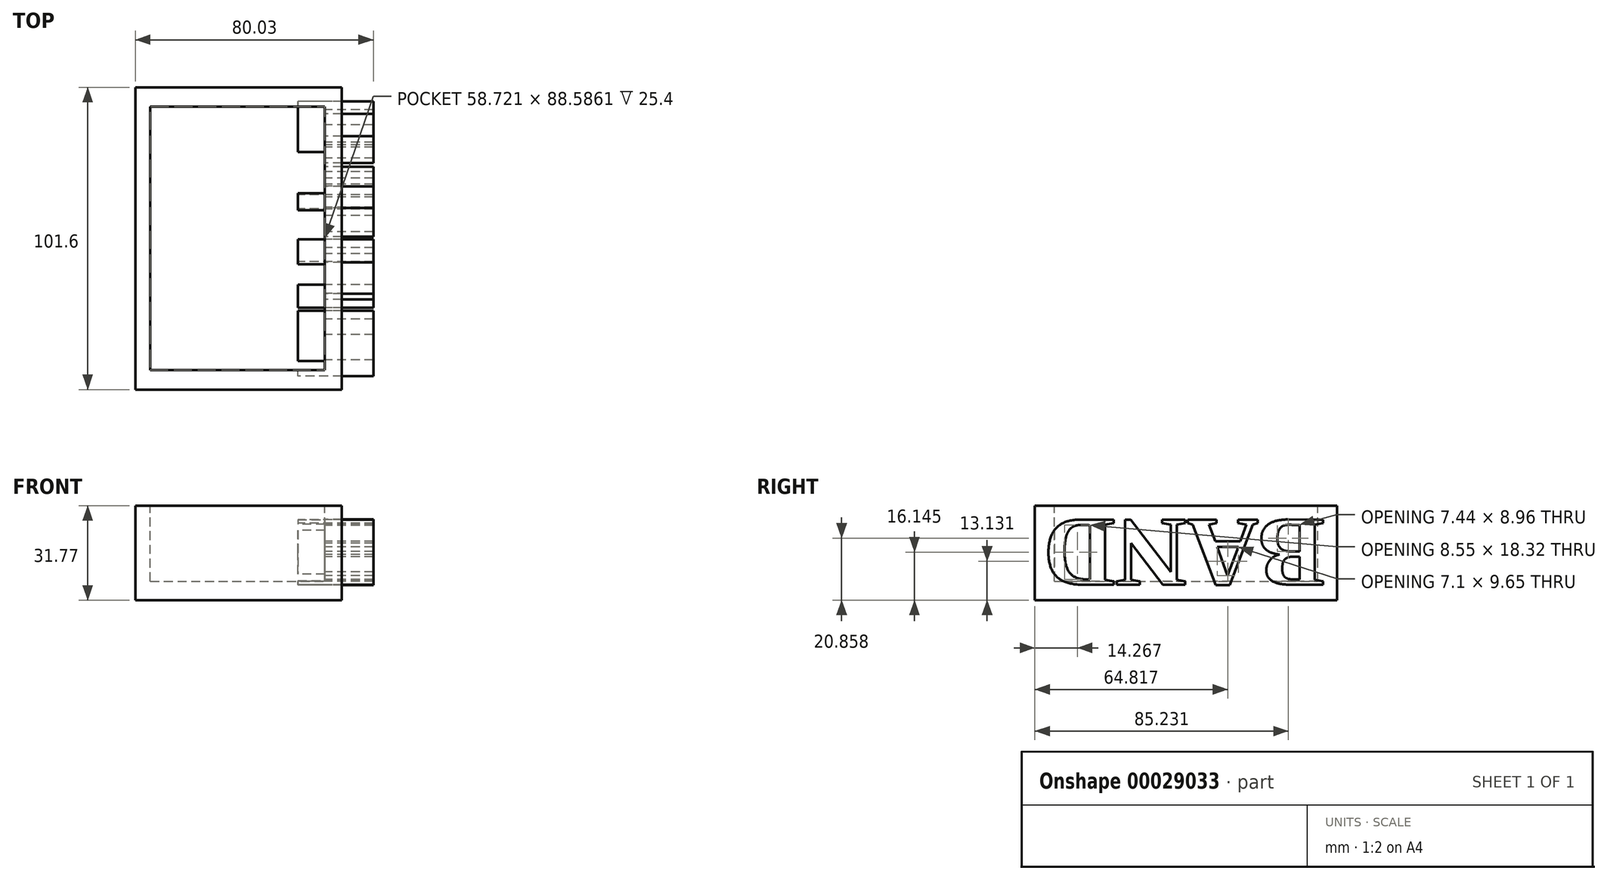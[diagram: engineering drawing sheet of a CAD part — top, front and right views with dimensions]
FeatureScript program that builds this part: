
annotation { "Feature Type Name" : "Feature", "Feature Type Description" : "" }
export const myFeature = defineFeature(function(context is Context, id is Id, definition is map)
    precondition{}
    {
        {
            var Q0;
            Q0=qCreatedBy(makeId("Front.planeOp"),FACE);
            var sketch = newSketch(context, id + "F0", { "sketchPlane" : qUnion([Q0])});
            skLineSegment(sketch, "E0.bottom", {"start": v(0, 0) * mm, "end": v(69.42, 0) * mm});
            skLineSegment(sketch, "E0.top", {"start": v(0, -19.07) * mm, "end": v(69.42, -19.07) * mm});
            skLineSegment(sketch, "E0.left", {"start": v(0, 0) * mm, "end": v(0, -19.07) * mm});
            skLineSegment(sketch, "E0.right", {"start": v(69.42, 0) * mm, "end": v(69.42, -19.07) * mm});
            skSolve(sketch);
        }
        {
            var Q0;
            Q0=makeQuery(id+"F0.imprint","IMPRINT",FACE,{"disambiguationData":[TD([[makeQuery(id+"F0.imprint","IMPRINT",EDGE,{"derivedFrom":sQuery(id+"F0.wireOp",EDGE,"E0.bottom")}),-1.0]])]});
            extrude(context, id + "F1", {"entities" : qUnion([Q0]), "depth" : 101.6 * mm});
        }
        {
            var Q0;
            Q0=makeQuery(id+"F1.opExtrude","SWEPT_BODY",BODY,{"disambiguationData":[OSD([sQuery(id+"F0.wireOp",EDGE,"E0.bottom"),sQuery(id+"F0.wireOp",EDGE,"E0.top"),sQuery(id+"F0.wireOp",EDGE,"E0.left"),sQuery(id+"F0.wireOp",EDGE,"E0.right")])]});
            transform(context, id + "F2", {"entities" : qUnion([Q0]), "transformType" : TransformType.TRANSLATION_3D, "dx" : -34.28 * mm, "dy" : 49.55 * mm, "dz" : 0 * mm, "makeCopy" : false});
        }
        {
            var Q0;
            Q0=makeQuery(id+"F1.opExtrude","SWEPT_FACE",FACE,{"disambiguationData":[OSD([sQuery(id+"F0.wireOp",EDGE,"E0.top")])]});
            extrude(context, id + "F3", {"entities" : qUnion([Q0]), "operationType" : NewBodyOperationType.ADD, "depth" : 12.7 * mm});
        }
        {
            var Q0;
            Q0=qCreatedBy(makeId("Top.planeOp"),FACE);
            var sketch = newSketch(context, id + "F4", { "sketchPlane" : qUnion([Q0])});
            skLineSegment(sketch, "E1.bottom", {"start": v(-34.3, -52.16) * mm, "end": v(24.42, -52.16) * mm});
            skLineSegment(sketch, "E1.top", {"start": v(-34.3, 36.42) * mm, "end": v(24.42, 36.42) * mm});
            skLineSegment(sketch, "E1.left", {"start": v(-34.3, -52.16) * mm, "end": v(-34.3, 36.42) * mm});
            skLineSegment(sketch, "E1.right", {"start": v(24.42, -52.16) * mm, "end": v(24.42, 36.42) * mm});
            skSolve(sketch);
        }
        {
            var Q0;
            Q0 = qSketchRegion(id + "F4", true);
            extrude(context, id + "F5", {"entities" : qUnion([Q0]), "oppositeDirection" : true, "depth" : 25.4 * mm});
        }
        {
            var Q0;
            Q0=makeQuery(id+"F5.opExtrude","SWEPT_BODY",BODY,{"disambiguationData":[OSD([sQuery(id+"F4.wireOp",EDGE,"E1.bottom"),sQuery(id+"F4.wireOp",EDGE,"E1.top"),sQuery(id+"F4.wireOp",EDGE,"E1.left"),sQuery(id+"F4.wireOp",EDGE,"E1.right")])]});
            transform(context, id + "F6", {"entities" : qUnion([Q0]), "transformType" : TransformType.TRANSLATION_3D, "dx" : 5.04 * mm, "dy" : 6.66 * mm, "dz" : 0 * mm, "makeCopy" : false});
        }
        {
            var Q0;
            Q0=makeQuery(id+"F5.opExtrude","SWEPT_BODY",BODY,{"disambiguationData":[OSD([sQuery(id+"F4.wireOp",EDGE,"E1.bottom"),sQuery(id+"F4.wireOp",EDGE,"E1.top"),sQuery(id+"F4.wireOp",EDGE,"E1.left"),sQuery(id+"F4.wireOp",EDGE,"E1.right")])]});
            var Q1;
            Q1=makeQuery(id+"F1.opExtrude","SWEPT_BODY",BODY,{"disambiguationData":[OSD([sQuery(id+"F0.wireOp",EDGE,"E0.bottom"),sQuery(id+"F0.wireOp",EDGE,"E0.top"),sQuery(id+"F0.wireOp",EDGE,"E0.left"),sQuery(id+"F0.wireOp",EDGE,"E0.right")])]});
            booleanBodies(context, id + "F7", {"operationType" : BooleanOperationType.SUBTRACTION, "tools" : qUnion([Q0]), "targets" : qUnion([Q1])});
        }
        {
            var Q0;
            {var subQ0=sQuery(id+"F0.wireOp",EDGE,"E0.left");Q0=makeQuery(id+"F3.boolean.opBoolean","MERGE",FACE,{"derivedFrom":[makeQuery(id+"F1.opExtrude","SWEPT_FACE",FACE,{"disambiguationData":[OSD([subQ0])]}),makeQuery(id+"F3.opExtrude","SWEPT_FACE",FACE,{"disambiguationData":[OSD([sQuery(id+"F0.wireOp",EDGE,"E0.top"),subQ0])]})]});}
            var sketch = newSketch(context, id + "F8", { "sketchPlane" : qUnion([Q0])});
            skText(sketch, "E2", { "text": "BAND", "fontName": "Tinos-Bold.ttf"});
            const initialGuessF8  = {"E2": [-0.0454, -0.02795, 1, 0, 0.02401]};
            skSetInitialGuess(sketch, initialGuessF8);
            skSolve(sketch);
        }
        {
            var Q0;
            Q0 = qSketchRegion(id + "F8", true);
            extrude(context, id + "F9", {"entities" : qUnion([Q0]), "depth" : 25.4 * mm});
        }
        {
            var Q0;
            Q0=makeQuery(id+"F9.opExtrude","SWEPT_BODY",BODY,{"disambiguationData":[OSD([sQuery(id+"F8.wireOp",EDGE,"E2.sketch_text.stroke-0"),sQuery(id+"F8.wireOp",EDGE,"E2.sketch_text.stroke-1"),sQuery(id+"F8.wireOp",EDGE,"E2.sketch_text.stroke-2"),sQuery(id+"F8.wireOp",EDGE,"E2.sketch_text.stroke-3"),sQuery(id+"F8.wireOp",EDGE,"E2.sketch_text.stroke-4"),sQuery(id+"F8.wireOp",EDGE,"E2.sketch_text.stroke-5"),sQuery(id+"F8.wireOp",EDGE,"E2.sketch_text.stroke-6"),sQuery(id+"F8.wireOp",EDGE,"E2.sketch_text.stroke-7"),sQuery(id+"F8.wireOp",EDGE,"E2.sketch_text.stroke-8"),sQuery(id+"F8.wireOp",EDGE,"E2.sketch_text.stroke-9"),sQuery(id+"F8.wireOp",EDGE,"E2.sketch_text.stroke-10"),sQuery(id+"F8.wireOp",EDGE,"E2.sketch_text.stroke-11"),sQuery(id+"F8.wireOp",EDGE,"E2.sketch_text.stroke-12"),sQuery(id+"F8.wireOp",EDGE,"E2.sketch_text.stroke-13"),sQuery(id+"F8.wireOp",EDGE,"E2.sketch_text.stroke-14"),sQuery(id+"F8.wireOp",EDGE,"E2.sketch_text.stroke-15"),sQuery(id+"F8.wireOp",EDGE,"E2.sketch_text.stroke-16"),sQuery(id+"F8.wireOp",EDGE,"E2.sketch_text.stroke-17"),sQuery(id+"F8.wireOp",EDGE,"E2.sketch_text.stroke-18"),sQuery(id+"F8.wireOp",EDGE,"E2.sketch_text.stroke-19"),sQuery(id+"F8.wireOp",EDGE,"E2.sketch_text.stroke-20"),sQuery(id+"F8.wireOp",EDGE,"E2.sketch_text.stroke-21"),sQuery(id+"F8.wireOp",EDGE,"E2.sketch_text.stroke-22"),sQuery(id+"F8.wireOp",EDGE,"E2.sketch_text.stroke-23"),sQuery(id+"F8.wireOp",EDGE,"E2.sketch_text.stroke-24"),sQuery(id+"F8.wireOp",EDGE,"E2.sketch_text.stroke-25"),sQuery(id+"F8.wireOp",EDGE,"E2.sketch_text.stroke-26"),sQuery(id+"F8.wireOp",EDGE,"E2.sketch_text.stroke-27"),sQuery(id+"F8.wireOp",EDGE,"E2.sketch_text.stroke-28"),sQuery(id+"F8.wireOp",EDGE,"E2.sketch_text.stroke-29")])]});
            var Q1;
            Q1=makeQuery(id+"F9.opExtrude","SWEPT_BODY",BODY,{"disambiguationData":[OSD([sQuery(id+"F8.wireOp",EDGE,"E2.sketch_text.stroke-30"),sQuery(id+"F8.wireOp",EDGE,"E2.sketch_text.stroke-31"),sQuery(id+"F8.wireOp",EDGE,"E2.sketch_text.stroke-32"),sQuery(id+"F8.wireOp",EDGE,"E2.sketch_text.stroke-33"),sQuery(id+"F8.wireOp",EDGE,"E2.sketch_text.stroke-34"),sQuery(id+"F8.wireOp",EDGE,"E2.sketch_text.stroke-35"),sQuery(id+"F8.wireOp",EDGE,"E2.sketch_text.stroke-36"),sQuery(id+"F8.wireOp",EDGE,"E2.sketch_text.stroke-37"),sQuery(id+"F8.wireOp",EDGE,"E2.sketch_text.stroke-38"),sQuery(id+"F8.wireOp",EDGE,"E2.sketch_text.stroke-39"),sQuery(id+"F8.wireOp",EDGE,"E2.sketch_text.stroke-40"),sQuery(id+"F8.wireOp",EDGE,"E2.sketch_text.stroke-41"),sQuery(id+"F8.wireOp",EDGE,"E2.sketch_text.stroke-42"),sQuery(id+"F8.wireOp",EDGE,"E2.sketch_text.stroke-43"),sQuery(id+"F8.wireOp",EDGE,"E2.sketch_text.stroke-44"),sQuery(id+"F8.wireOp",EDGE,"E2.sketch_text.stroke-45"),sQuery(id+"F8.wireOp",EDGE,"E2.sketch_text.stroke-46"),sQuery(id+"F8.wireOp",EDGE,"E2.sketch_text.stroke-47"),sQuery(id+"F8.wireOp",EDGE,"E2.sketch_text.stroke-48")])]});
            var Q2;
            Q2=makeQuery(id+"F9.opExtrude","SWEPT_BODY",BODY,{"disambiguationData":[OSD([sQuery(id+"F8.wireOp",EDGE,"E2.sketch_text.stroke-49"),sQuery(id+"F8.wireOp",EDGE,"E2.sketch_text.stroke-50"),sQuery(id+"F8.wireOp",EDGE,"E2.sketch_text.stroke-51"),sQuery(id+"F8.wireOp",EDGE,"E2.sketch_text.stroke-52"),sQuery(id+"F8.wireOp",EDGE,"E2.sketch_text.stroke-53"),sQuery(id+"F8.wireOp",EDGE,"E2.sketch_text.stroke-54"),sQuery(id+"F8.wireOp",EDGE,"E2.sketch_text.stroke-55"),sQuery(id+"F8.wireOp",EDGE,"E2.sketch_text.stroke-56"),sQuery(id+"F8.wireOp",EDGE,"E2.sketch_text.stroke-57"),sQuery(id+"F8.wireOp",EDGE,"E2.sketch_text.stroke-58"),sQuery(id+"F8.wireOp",EDGE,"E2.sketch_text.stroke-59"),sQuery(id+"F8.wireOp",EDGE,"E2.sketch_text.stroke-60"),sQuery(id+"F8.wireOp",EDGE,"E2.sketch_text.stroke-61"),sQuery(id+"F8.wireOp",EDGE,"E2.sketch_text.stroke-62"),sQuery(id+"F8.wireOp",EDGE,"E2.sketch_text.stroke-63"),sQuery(id+"F8.wireOp",EDGE,"E2.sketch_text.stroke-64"),sQuery(id+"F8.wireOp",EDGE,"E2.sketch_text.stroke-65"),sQuery(id+"F8.wireOp",EDGE,"E2.sketch_text.stroke-66"),sQuery(id+"F8.wireOp",EDGE,"E2.sketch_text.stroke-67"),sQuery(id+"F8.wireOp",EDGE,"E2.sketch_text.stroke-68")])]});
            var Q3;
            Q3=makeQuery(id+"F9.opExtrude","SWEPT_BODY",BODY,{"disambiguationData":[OSD([sQuery(id+"F8.wireOp",EDGE,"E2.sketch_text.stroke-69"),sQuery(id+"F8.wireOp",EDGE,"E2.sketch_text.stroke-70"),sQuery(id+"F8.wireOp",EDGE,"E2.sketch_text.stroke-71"),sQuery(id+"F8.wireOp",EDGE,"E2.sketch_text.stroke-72"),sQuery(id+"F8.wireOp",EDGE,"E2.sketch_text.stroke-73"),sQuery(id+"F8.wireOp",EDGE,"E2.sketch_text.stroke-74"),sQuery(id+"F8.wireOp",EDGE,"E2.sketch_text.stroke-75"),sQuery(id+"F8.wireOp",EDGE,"E2.sketch_text.stroke-76"),sQuery(id+"F8.wireOp",EDGE,"E2.sketch_text.stroke-77"),sQuery(id+"F8.wireOp",EDGE,"E2.sketch_text.stroke-78"),sQuery(id+"F8.wireOp",EDGE,"E2.sketch_text.stroke-79"),sQuery(id+"F8.wireOp",EDGE,"E2.sketch_text.stroke-80"),sQuery(id+"F8.wireOp",EDGE,"E2.sketch_text.stroke-81"),sQuery(id+"F8.wireOp",EDGE,"E2.sketch_text.stroke-82"),sQuery(id+"F8.wireOp",EDGE,"E2.sketch_text.stroke-83"),sQuery(id+"F8.wireOp",EDGE,"E2.sketch_text.stroke-84"),sQuery(id+"F8.wireOp",EDGE,"E2.sketch_text.stroke-85"),sQuery(id+"F8.wireOp",EDGE,"E2.sketch_text.stroke-86"),sQuery(id+"F8.wireOp",EDGE,"E2.sketch_text.stroke-87"),sQuery(id+"F8.wireOp",EDGE,"E2.sketch_text.stroke-88")])]});
            var Q4;
            Q4=makeQuery(id+"F1.opExtrude","SWEPT_EDGE",EDGE,{"disambiguationData":[OSD([sQuery(id+"F0.wireOp",EDGE,"E0.bottom"),sQuery(id+"F0.wireOp",EDGE,"E0.left")])]});
            transform(context, id + "F10", {"entities" : qUnion([Q0, Q1, Q2, Q3]), "transformType" : TransformType.ROTATION, "transformAxis" : qUnion([Q4]), "angle" : 180 * degree, "makeCopy" : false});
        }
        {
            var Q0;
            Q0=makeQuery(id+"F9.opExtrude","SWEPT_BODY",BODY,{"disambiguationData":[OSD([sQuery(id+"F8.wireOp",EDGE,"E2.sketch_text.stroke-69"),sQuery(id+"F8.wireOp",EDGE,"E2.sketch_text.stroke-70"),sQuery(id+"F8.wireOp",EDGE,"E2.sketch_text.stroke-71"),sQuery(id+"F8.wireOp",EDGE,"E2.sketch_text.stroke-72"),sQuery(id+"F8.wireOp",EDGE,"E2.sketch_text.stroke-73"),sQuery(id+"F8.wireOp",EDGE,"E2.sketch_text.stroke-74"),sQuery(id+"F8.wireOp",EDGE,"E2.sketch_text.stroke-75"),sQuery(id+"F8.wireOp",EDGE,"E2.sketch_text.stroke-76"),sQuery(id+"F8.wireOp",EDGE,"E2.sketch_text.stroke-77"),sQuery(id+"F8.wireOp",EDGE,"E2.sketch_text.stroke-78"),sQuery(id+"F8.wireOp",EDGE,"E2.sketch_text.stroke-79"),sQuery(id+"F8.wireOp",EDGE,"E2.sketch_text.stroke-80"),sQuery(id+"F8.wireOp",EDGE,"E2.sketch_text.stroke-81"),sQuery(id+"F8.wireOp",EDGE,"E2.sketch_text.stroke-82"),sQuery(id+"F8.wireOp",EDGE,"E2.sketch_text.stroke-83"),sQuery(id+"F8.wireOp",EDGE,"E2.sketch_text.stroke-84"),sQuery(id+"F8.wireOp",EDGE,"E2.sketch_text.stroke-85"),sQuery(id+"F8.wireOp",EDGE,"E2.sketch_text.stroke-86"),sQuery(id+"F8.wireOp",EDGE,"E2.sketch_text.stroke-87"),sQuery(id+"F8.wireOp",EDGE,"E2.sketch_text.stroke-88")])]});
            var Q1;
            Q1=makeQuery(id+"F9.opExtrude","SWEPT_BODY",BODY,{"disambiguationData":[OSD([sQuery(id+"F8.wireOp",EDGE,"E2.sketch_text.stroke-49"),sQuery(id+"F8.wireOp",EDGE,"E2.sketch_text.stroke-50"),sQuery(id+"F8.wireOp",EDGE,"E2.sketch_text.stroke-51"),sQuery(id+"F8.wireOp",EDGE,"E2.sketch_text.stroke-52"),sQuery(id+"F8.wireOp",EDGE,"E2.sketch_text.stroke-53"),sQuery(id+"F8.wireOp",EDGE,"E2.sketch_text.stroke-54"),sQuery(id+"F8.wireOp",EDGE,"E2.sketch_text.stroke-55"),sQuery(id+"F8.wireOp",EDGE,"E2.sketch_text.stroke-56"),sQuery(id+"F8.wireOp",EDGE,"E2.sketch_text.stroke-57"),sQuery(id+"F8.wireOp",EDGE,"E2.sketch_text.stroke-58"),sQuery(id+"F8.wireOp",EDGE,"E2.sketch_text.stroke-59"),sQuery(id+"F8.wireOp",EDGE,"E2.sketch_text.stroke-60"),sQuery(id+"F8.wireOp",EDGE,"E2.sketch_text.stroke-61"),sQuery(id+"F8.wireOp",EDGE,"E2.sketch_text.stroke-62"),sQuery(id+"F8.wireOp",EDGE,"E2.sketch_text.stroke-63"),sQuery(id+"F8.wireOp",EDGE,"E2.sketch_text.stroke-64"),sQuery(id+"F8.wireOp",EDGE,"E2.sketch_text.stroke-65"),sQuery(id+"F8.wireOp",EDGE,"E2.sketch_text.stroke-66"),sQuery(id+"F8.wireOp",EDGE,"E2.sketch_text.stroke-67"),sQuery(id+"F8.wireOp",EDGE,"E2.sketch_text.stroke-68")])]});
            var Q2;
            Q2=makeQuery(id+"F9.opExtrude","SWEPT_BODY",BODY,{"disambiguationData":[OSD([sQuery(id+"F8.wireOp",EDGE,"E2.sketch_text.stroke-30"),sQuery(id+"F8.wireOp",EDGE,"E2.sketch_text.stroke-31"),sQuery(id+"F8.wireOp",EDGE,"E2.sketch_text.stroke-32"),sQuery(id+"F8.wireOp",EDGE,"E2.sketch_text.stroke-33"),sQuery(id+"F8.wireOp",EDGE,"E2.sketch_text.stroke-34"),sQuery(id+"F8.wireOp",EDGE,"E2.sketch_text.stroke-35"),sQuery(id+"F8.wireOp",EDGE,"E2.sketch_text.stroke-36"),sQuery(id+"F8.wireOp",EDGE,"E2.sketch_text.stroke-37"),sQuery(id+"F8.wireOp",EDGE,"E2.sketch_text.stroke-38"),sQuery(id+"F8.wireOp",EDGE,"E2.sketch_text.stroke-39"),sQuery(id+"F8.wireOp",EDGE,"E2.sketch_text.stroke-40"),sQuery(id+"F8.wireOp",EDGE,"E2.sketch_text.stroke-41"),sQuery(id+"F8.wireOp",EDGE,"E2.sketch_text.stroke-42"),sQuery(id+"F8.wireOp",EDGE,"E2.sketch_text.stroke-43"),sQuery(id+"F8.wireOp",EDGE,"E2.sketch_text.stroke-44"),sQuery(id+"F8.wireOp",EDGE,"E2.sketch_text.stroke-45"),sQuery(id+"F8.wireOp",EDGE,"E2.sketch_text.stroke-46"),sQuery(id+"F8.wireOp",EDGE,"E2.sketch_text.stroke-47"),sQuery(id+"F8.wireOp",EDGE,"E2.sketch_text.stroke-48")])]});
            var Q3;
            Q3=makeQuery(id+"F9.opExtrude","SWEPT_BODY",BODY,{"disambiguationData":[OSD([sQuery(id+"F8.wireOp",EDGE,"E2.sketch_text.stroke-0"),sQuery(id+"F8.wireOp",EDGE,"E2.sketch_text.stroke-1"),sQuery(id+"F8.wireOp",EDGE,"E2.sketch_text.stroke-2"),sQuery(id+"F8.wireOp",EDGE,"E2.sketch_text.stroke-3"),sQuery(id+"F8.wireOp",EDGE,"E2.sketch_text.stroke-4"),sQuery(id+"F8.wireOp",EDGE,"E2.sketch_text.stroke-5"),sQuery(id+"F8.wireOp",EDGE,"E2.sketch_text.stroke-6"),sQuery(id+"F8.wireOp",EDGE,"E2.sketch_text.stroke-7"),sQuery(id+"F8.wireOp",EDGE,"E2.sketch_text.stroke-8"),sQuery(id+"F8.wireOp",EDGE,"E2.sketch_text.stroke-9"),sQuery(id+"F8.wireOp",EDGE,"E2.sketch_text.stroke-10"),sQuery(id+"F8.wireOp",EDGE,"E2.sketch_text.stroke-11"),sQuery(id+"F8.wireOp",EDGE,"E2.sketch_text.stroke-12"),sQuery(id+"F8.wireOp",EDGE,"E2.sketch_text.stroke-13"),sQuery(id+"F8.wireOp",EDGE,"E2.sketch_text.stroke-14"),sQuery(id+"F8.wireOp",EDGE,"E2.sketch_text.stroke-15"),sQuery(id+"F8.wireOp",EDGE,"E2.sketch_text.stroke-16"),sQuery(id+"F8.wireOp",EDGE,"E2.sketch_text.stroke-17"),sQuery(id+"F8.wireOp",EDGE,"E2.sketch_text.stroke-18"),sQuery(id+"F8.wireOp",EDGE,"E2.sketch_text.stroke-19"),sQuery(id+"F8.wireOp",EDGE,"E2.sketch_text.stroke-20"),sQuery(id+"F8.wireOp",EDGE,"E2.sketch_text.stroke-21"),sQuery(id+"F8.wireOp",EDGE,"E2.sketch_text.stroke-22"),sQuery(id+"F8.wireOp",EDGE,"E2.sketch_text.stroke-23"),sQuery(id+"F8.wireOp",EDGE,"E2.sketch_text.stroke-24"),sQuery(id+"F8.wireOp",EDGE,"E2.sketch_text.stroke-25"),sQuery(id+"F8.wireOp",EDGE,"E2.sketch_text.stroke-26"),sQuery(id+"F8.wireOp",EDGE,"E2.sketch_text.stroke-27"),sQuery(id+"F8.wireOp",EDGE,"E2.sketch_text.stroke-28"),sQuery(id+"F8.wireOp",EDGE,"E2.sketch_text.stroke-29")])]});
            transform(context, id + "F11", {"entities" : qUnion([Q0, Q1, Q2, Q3]), "transformType" : TransformType.TRANSLATION_3D, "dx" : 54.63 * mm, "dy" : 0 * mm, "dz" : -32.7 * mm, "makeCopy" : false});
        }
        {
            var Q0;
            Q0=makeQuery(id+"F1.opExtrude","SWEPT_FACE",FACE,{"disambiguationData":[OSD([sQuery(id+"F0.wireOp",EDGE,"E0.bottom")])]});
            var sketch = newSketch(context, id + "F12", { "sketchPlane" : qUnion([Q0])});
            skLineSegment(sketch, "E3.bottom", {"start": v(15.94, 43.08) * mm, "end": v(29.46, 43.08) * mm});
            skLineSegment(sketch, "E3.top", {"start": v(15.94, -45.5) * mm, "end": v(29.46, -45.5) * mm});
            skLineSegment(sketch, "E3.left", {"start": v(15.94, 43.08) * mm, "end": v(15.94, -45.5) * mm});
            skLineSegment(sketch, "E3.right", {"start": v(29.46, 43.08) * mm, "end": v(29.46, -45.5) * mm});
            skSolve(sketch);
        }
        {
            var Q0;
            Q0=makeQuery(id+"F12.imprint","IMPRINT",FACE,{"disambiguationData":[TD([[makeQuery(id+"F12.imprint","IMPRINT",EDGE,{"derivedFrom":sQuery(id+"F12.wireOp",EDGE,"E3.bottom")}),-1.0]])]});
            extrude(context, id + "F13", {"entities" : qUnion([Q0]), "oppositeDirection" : true, "depth" : 25.4 * mm});
        }
        {
            var Q0;
            Q0=makeQuery(id+"F13.opExtrude","SWEPT_BODY",BODY,{"disambiguationData":[OSD([sQuery(id+"F12.wireOp",EDGE,"E3.bottom"),sQuery(id+"F12.wireOp",EDGE,"E3.top"),sQuery(id+"F12.wireOp",EDGE,"E3.left"),sQuery(id+"F12.wireOp",EDGE,"E3.right")])]});
            var Q1;
            Q1=makeQuery(id+"F9.opExtrude","SWEPT_BODY",BODY,{"disambiguationData":[OSD([sQuery(id+"F8.wireOp",EDGE,"E2.sketch_text.stroke-0"),sQuery(id+"F8.wireOp",EDGE,"E2.sketch_text.stroke-1"),sQuery(id+"F8.wireOp",EDGE,"E2.sketch_text.stroke-2"),sQuery(id+"F8.wireOp",EDGE,"E2.sketch_text.stroke-3"),sQuery(id+"F8.wireOp",EDGE,"E2.sketch_text.stroke-4"),sQuery(id+"F8.wireOp",EDGE,"E2.sketch_text.stroke-5"),sQuery(id+"F8.wireOp",EDGE,"E2.sketch_text.stroke-6"),sQuery(id+"F8.wireOp",EDGE,"E2.sketch_text.stroke-7"),sQuery(id+"F8.wireOp",EDGE,"E2.sketch_text.stroke-8"),sQuery(id+"F8.wireOp",EDGE,"E2.sketch_text.stroke-9"),sQuery(id+"F8.wireOp",EDGE,"E2.sketch_text.stroke-10"),sQuery(id+"F8.wireOp",EDGE,"E2.sketch_text.stroke-11"),sQuery(id+"F8.wireOp",EDGE,"E2.sketch_text.stroke-12"),sQuery(id+"F8.wireOp",EDGE,"E2.sketch_text.stroke-13"),sQuery(id+"F8.wireOp",EDGE,"E2.sketch_text.stroke-14"),sQuery(id+"F8.wireOp",EDGE,"E2.sketch_text.stroke-15"),sQuery(id+"F8.wireOp",EDGE,"E2.sketch_text.stroke-16"),sQuery(id+"F8.wireOp",EDGE,"E2.sketch_text.stroke-17"),sQuery(id+"F8.wireOp",EDGE,"E2.sketch_text.stroke-18"),sQuery(id+"F8.wireOp",EDGE,"E2.sketch_text.stroke-19"),sQuery(id+"F8.wireOp",EDGE,"E2.sketch_text.stroke-20"),sQuery(id+"F8.wireOp",EDGE,"E2.sketch_text.stroke-21"),sQuery(id+"F8.wireOp",EDGE,"E2.sketch_text.stroke-22"),sQuery(id+"F8.wireOp",EDGE,"E2.sketch_text.stroke-23"),sQuery(id+"F8.wireOp",EDGE,"E2.sketch_text.stroke-24"),sQuery(id+"F8.wireOp",EDGE,"E2.sketch_text.stroke-25"),sQuery(id+"F8.wireOp",EDGE,"E2.sketch_text.stroke-26"),sQuery(id+"F8.wireOp",EDGE,"E2.sketch_text.stroke-27"),sQuery(id+"F8.wireOp",EDGE,"E2.sketch_text.stroke-28"),sQuery(id+"F8.wireOp",EDGE,"E2.sketch_text.stroke-29")])]});
            var Q2;
            Q2=makeQuery(id+"F9.opExtrude","SWEPT_BODY",BODY,{"disambiguationData":[OSD([sQuery(id+"F8.wireOp",EDGE,"E2.sketch_text.stroke-30"),sQuery(id+"F8.wireOp",EDGE,"E2.sketch_text.stroke-31"),sQuery(id+"F8.wireOp",EDGE,"E2.sketch_text.stroke-32"),sQuery(id+"F8.wireOp",EDGE,"E2.sketch_text.stroke-33"),sQuery(id+"F8.wireOp",EDGE,"E2.sketch_text.stroke-34"),sQuery(id+"F8.wireOp",EDGE,"E2.sketch_text.stroke-35"),sQuery(id+"F8.wireOp",EDGE,"E2.sketch_text.stroke-36"),sQuery(id+"F8.wireOp",EDGE,"E2.sketch_text.stroke-37"),sQuery(id+"F8.wireOp",EDGE,"E2.sketch_text.stroke-38"),sQuery(id+"F8.wireOp",EDGE,"E2.sketch_text.stroke-39"),sQuery(id+"F8.wireOp",EDGE,"E2.sketch_text.stroke-40"),sQuery(id+"F8.wireOp",EDGE,"E2.sketch_text.stroke-41"),sQuery(id+"F8.wireOp",EDGE,"E2.sketch_text.stroke-42"),sQuery(id+"F8.wireOp",EDGE,"E2.sketch_text.stroke-43"),sQuery(id+"F8.wireOp",EDGE,"E2.sketch_text.stroke-44"),sQuery(id+"F8.wireOp",EDGE,"E2.sketch_text.stroke-45"),sQuery(id+"F8.wireOp",EDGE,"E2.sketch_text.stroke-46"),sQuery(id+"F8.wireOp",EDGE,"E2.sketch_text.stroke-47"),sQuery(id+"F8.wireOp",EDGE,"E2.sketch_text.stroke-48")])]});
            var Q3;
            Q3=makeQuery(id+"F9.opExtrude","SWEPT_BODY",BODY,{"disambiguationData":[OSD([sQuery(id+"F8.wireOp",EDGE,"E2.sketch_text.stroke-49"),sQuery(id+"F8.wireOp",EDGE,"E2.sketch_text.stroke-50"),sQuery(id+"F8.wireOp",EDGE,"E2.sketch_text.stroke-51"),sQuery(id+"F8.wireOp",EDGE,"E2.sketch_text.stroke-52"),sQuery(id+"F8.wireOp",EDGE,"E2.sketch_text.stroke-53"),sQuery(id+"F8.wireOp",EDGE,"E2.sketch_text.stroke-54"),sQuery(id+"F8.wireOp",EDGE,"E2.sketch_text.stroke-55"),sQuery(id+"F8.wireOp",EDGE,"E2.sketch_text.stroke-56"),sQuery(id+"F8.wireOp",EDGE,"E2.sketch_text.stroke-57"),sQuery(id+"F8.wireOp",EDGE,"E2.sketch_text.stroke-58"),sQuery(id+"F8.wireOp",EDGE,"E2.sketch_text.stroke-59"),sQuery(id+"F8.wireOp",EDGE,"E2.sketch_text.stroke-60"),sQuery(id+"F8.wireOp",EDGE,"E2.sketch_text.stroke-61"),sQuery(id+"F8.wireOp",EDGE,"E2.sketch_text.stroke-62"),sQuery(id+"F8.wireOp",EDGE,"E2.sketch_text.stroke-63"),sQuery(id+"F8.wireOp",EDGE,"E2.sketch_text.stroke-64"),sQuery(id+"F8.wireOp",EDGE,"E2.sketch_text.stroke-65"),sQuery(id+"F8.wireOp",EDGE,"E2.sketch_text.stroke-66"),sQuery(id+"F8.wireOp",EDGE,"E2.sketch_text.stroke-67"),sQuery(id+"F8.wireOp",EDGE,"E2.sketch_text.stroke-68")])]});
            var Q4;
            Q4=makeQuery(id+"F9.opExtrude","SWEPT_BODY",BODY,{"disambiguationData":[OSD([sQuery(id+"F8.wireOp",EDGE,"E2.sketch_text.stroke-69"),sQuery(id+"F8.wireOp",EDGE,"E2.sketch_text.stroke-70"),sQuery(id+"F8.wireOp",EDGE,"E2.sketch_text.stroke-71"),sQuery(id+"F8.wireOp",EDGE,"E2.sketch_text.stroke-72"),sQuery(id+"F8.wireOp",EDGE,"E2.sketch_text.stroke-73"),sQuery(id+"F8.wireOp",EDGE,"E2.sketch_text.stroke-74"),sQuery(id+"F8.wireOp",EDGE,"E2.sketch_text.stroke-75"),sQuery(id+"F8.wireOp",EDGE,"E2.sketch_text.stroke-76"),sQuery(id+"F8.wireOp",EDGE,"E2.sketch_text.stroke-77"),sQuery(id+"F8.wireOp",EDGE,"E2.sketch_text.stroke-78"),sQuery(id+"F8.wireOp",EDGE,"E2.sketch_text.stroke-79"),sQuery(id+"F8.wireOp",EDGE,"E2.sketch_text.stroke-80"),sQuery(id+"F8.wireOp",EDGE,"E2.sketch_text.stroke-81"),sQuery(id+"F8.wireOp",EDGE,"E2.sketch_text.stroke-82"),sQuery(id+"F8.wireOp",EDGE,"E2.sketch_text.stroke-83"),sQuery(id+"F8.wireOp",EDGE,"E2.sketch_text.stroke-84"),sQuery(id+"F8.wireOp",EDGE,"E2.sketch_text.stroke-85"),sQuery(id+"F8.wireOp",EDGE,"E2.sketch_text.stroke-86"),sQuery(id+"F8.wireOp",EDGE,"E2.sketch_text.stroke-87"),sQuery(id+"F8.wireOp",EDGE,"E2.sketch_text.stroke-88")])]});
            booleanBodies(context, id + "F14", {"operationType" : BooleanOperationType.SUBTRACTION, "tools" : qUnion([Q0]), "targets" : qUnion([Q1, Q2, Q3, Q4])});
        }
    });
